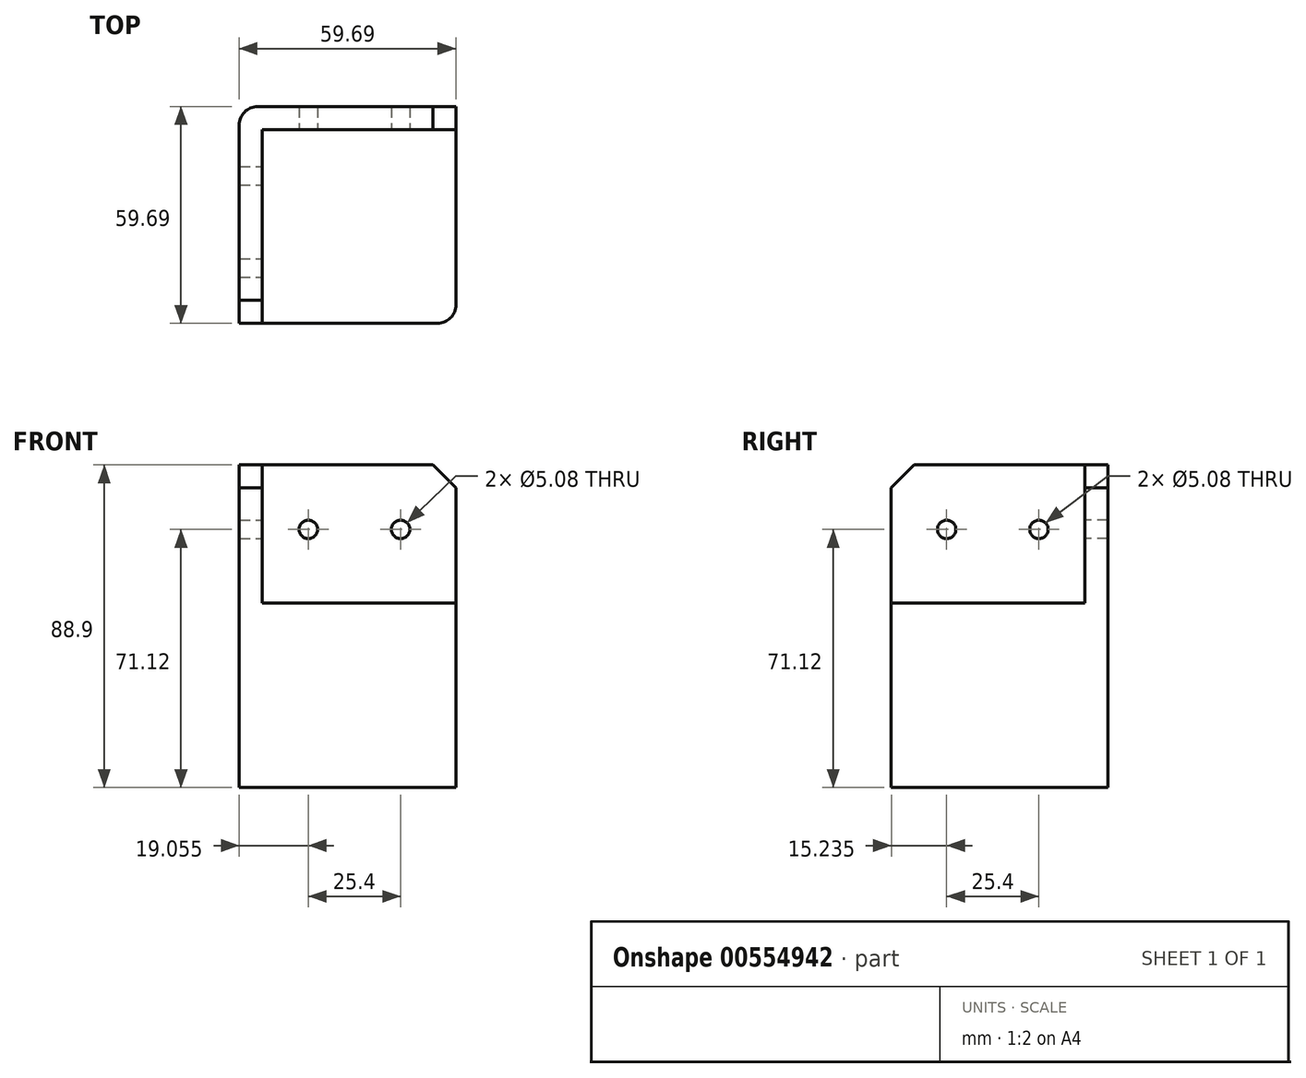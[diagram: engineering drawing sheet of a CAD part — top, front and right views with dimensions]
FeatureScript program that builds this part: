
annotation { "Feature Type Name" : "Feature", "Feature Type Description" : "" }
export const myFeature = defineFeature(function(context is Context, id is Id, definition is map)
    precondition{}
    {
        {
            var Q0;
            Q0=qCreatedBy(makeId("Top.planeOp"),FACE);
            var sketch = newSketch(context, id + "F0", { "sketchPlane" : qUnion([Q0])});
            skLineSegment(sketch, "E0.bottom", {"start": v(29.85, -29.84) * mm, "end": v(-29.84, -29.85) * mm});
            skLineSegment(sketch, "E0.top", {"start": v(29.84, 29.85) * mm, "end": v(-29.85, 29.84) * mm});
            skLineSegment(sketch, "E0.left", {"start": v(29.85, -29.84) * mm, "end": v(29.84, 29.85) * mm});
            skLineSegment(sketch, "E0.right", {"start": v(-29.84, -29.85) * mm, "end": v(-29.85, 29.84) * mm});
            skPoint(sketch, "E0.middle", {"position": v(0, 0) * mm});
            skSolve(sketch);
        }
        {
            var Q0;
            Q0 = qSketchRegion(id + "F0", true);
            extrude(context, id + "F1", {"entities" : qUnion([Q0]), "depth" : 25.4 * mm, "offsetDistance" : 25.4 * mm, "hasSecondDirection" : true, "secondDirectionOppositeDirection" : true, "secondDirectionDepth" : 25.4 * mm});
        }
        {
            var Q0;
            Q0=makeQuery(id+"F1.opExtrude","CAP_FACE",FACE,{"disambiguationData":[OSD([sQuery(id+"F0.wireOp",EDGE,"E0.bottom"),sQuery(id+"F0.wireOp",EDGE,"E0.top"),sQuery(id+"F0.wireOp",EDGE,"E0.left"),sQuery(id+"F0.wireOp",EDGE,"E0.right")])],"isStart":false});
            var sketch = newSketch(context, id + "F2", { "sketchPlane" : qUnion([Q0])});
            skLineSegment(sketch, "E1", {"start": v(29.85, 23.5) * mm, "end": v(-23.5, 23.5) * mm});
            skLineSegment(sketch, "E2", {"start": v(-23.5, 23.5) * mm, "end": v(-23.5, -29.85) * mm});
            skSolve(sketch);
        }
        {
            var Q0;
            Q0 = qSketchRegion(id + "F2", true);
            var Q1;
            {var subQ3=sQuery(id+"F2.wireOp",EDGE,"E1");Q1=makeQuery(id+"F2.imprint","IMPRINT",FACE,{"disambiguationData":[TD([[makeQuery(id+"F2.imprint","IMPRINT",EDGE,{"derivedFrom":subQ3}),-1.0]])]});}
            extrude(context, id + "F3", {"entities" : qUnion([Q0, Q1]), "operationType" : NewBodyOperationType.ADD, "depth" : 38.1 * mm, "offsetDistance" : 25.4 * mm});
        }
        {
            var Q0;
            Q0=makeQuery(id+"F3.opExtrude","CAP_EDGE",EDGE,{"disambiguationData":[OSD([sQuery(id+"F0.wireOp",EDGE,"E0.bottom")])],"isStart":false});
            var Q1;
            Q1=makeQuery(id+"F3.opExtrude","CAP_EDGE",EDGE,{"disambiguationData":[OSD([sQuery(id+"F0.wireOp",EDGE,"E0.left")])],"isStart":false});
            var Q2;
            Q2=makeQuery(id+"FbmWTuriZFgiiim_1.1.F3.opExtrude","CAP_EDGE",EDGE,{"disambiguationData":[OSD([sQuery(id+"F0.wireOp",EDGE,"E0.bottom")])],"isStart":false});
            var Q3;
            Q3=makeQuery(id+"FbmWTuriZFgiiim_1.1.F3.opExtrude","CAP_EDGE",EDGE,{"disambiguationData":[OSD([sQuery(id+"F0.wireOp",EDGE,"E0.left")])],"isStart":false});
            chamfer(context, id + "F4", {"entities" : qUnion([Q0, Q1, Q2, Q3]), "width" : 6.35 * mm, "tangentPropagation" : true});
        }
        {
            var Q0;
            Q0=makeQuery(id+"F1.opExtrude","SWEPT_EDGE",EDGE,{"disambiguationData":[OSD([sQuery(id+"F0.wireOp",EDGE,"E0.bottom"),sQuery(id+"F0.wireOp",EDGE,"E0.left")])]});
            fillet(context, id + "F5", {"entities" : qUnion([Q0]), "radius" : 5.08 * mm, "tangentPropagation" : true, "allowEdgeOverflow" : false});
        }
        {
            var Q0;
            {var subQ0=sQuery(id+"F0.wireOp",EDGE,"E0.right");var subQ1=sQuery(id+"F0.wireOp",EDGE,"E0.top");Q0=makeQuery(id+"FbmWTuriZFgiiim_1.1.F3.boolean.opBoolean","MERGE",EDGE,{"derivedFrom":[makeQuery(id+"F3.boolean.opBoolean","MERGE",EDGE,{"derivedFrom":[makeQuery(id+"F1.opExtrude","SWEPT_EDGE",EDGE,{"disambiguationData":[OSD([subQ1,subQ0])]}),makeQuery(id+"F3.opExtrude","SWEPT_EDGE",EDGE,{"disambiguationData":[OSD([subQ1,subQ0])]})]}),makeQuery(id+"FbmWTuriZFgiiim_1.1.F3.opExtrude","SWEPT_EDGE",EDGE,{"disambiguationData":[OSD([subQ1,subQ0])]})]});}
            fillet(context, id + "F6", {"entities" : qUnion([Q0]), "radius" : 5.08 * mm, "tangentPropagation" : true, "allowEdgeOverflow" : false});
        }
        {
            var Q0;
            Q0=makeQuery(id+"F3.opExtrude","SWEPT_FACE",FACE,{"disambiguationData":[OSD([sQuery(id+"F2.wireOp",EDGE,"E1")])]});
            var sketch = newSketch(context, id + "F7", { "sketchPlane" : qUnion([Q0])});
            skCircle(sketch, "E3", {"center": v(-10.8, 45.72) * mm, "radius": 2.54 * mm});
            skCircle(sketch, "E4", {"center": v(14.6, 45.72) * mm, "radius": 2.54 * mm});
            skSolve(sketch);
        }
        {
            var Q0;
            Q0 = qSketchRegion(id + "F7", true);
            extrude(context, id + "F8", {"entities" : qUnion([Q0]), "operationType" : NewBodyOperationType.REMOVE, "oppositeDirection" : true, "depth" : 25.4 * mm, "offsetDistance" : 25.4 * mm});
        }
        {
            var Q0;
            Q0=makeQuery(id+"F3.opExtrude","SWEPT_FACE",FACE,{"disambiguationData":[OSD([sQuery(id+"F2.wireOp",EDGE,"E2")])]});
            var sketch = newSketch(context, id + "F9", { "sketchPlane" : qUnion([Q0])});
            skCircle(sketch, "E5", {"center": v(-14.6, 45.72) * mm, "radius": 2.54 * mm});
            skCircle(sketch, "E6", {"center": v(10.8, 45.72) * mm, "radius": 2.54 * mm});
            skSolve(sketch);
        }
        {
            var Q0;
            Q0 = qSketchRegion(id + "F9", true);
            extrude(context, id + "F10", {"entities" : qUnion([Q0]), "operationType" : NewBodyOperationType.REMOVE, "oppositeDirection" : true, "depth" : 25.4 * mm, "offsetDistance" : 25.4 * mm});
        }
    });
